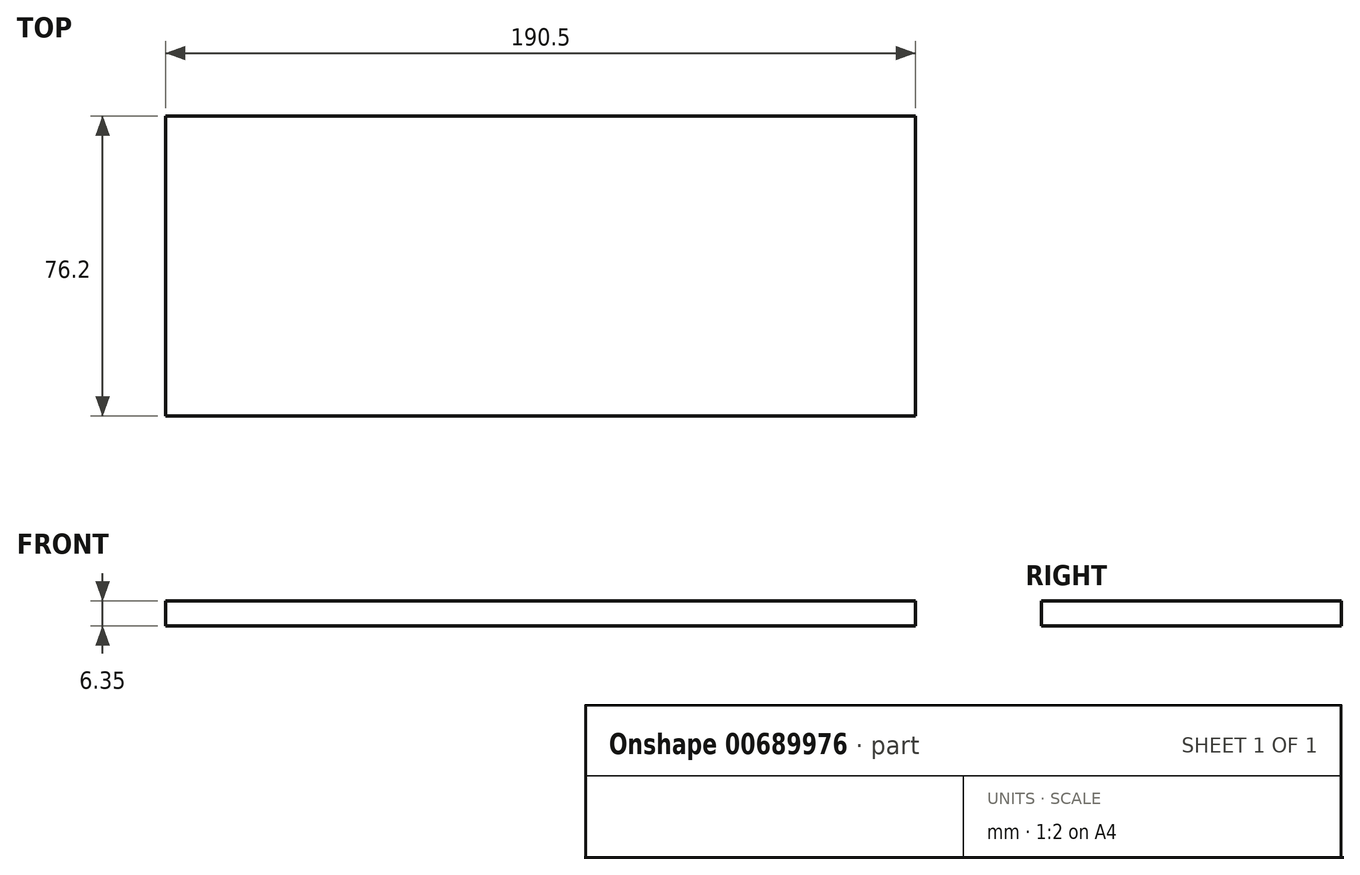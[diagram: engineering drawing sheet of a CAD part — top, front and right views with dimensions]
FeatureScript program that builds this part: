
annotation { "Feature Type Name" : "Feature", "Feature Type Description" : "" }
export const myFeature = defineFeature(function(context is Context, id is Id, definition is map)
    precondition{}
    {
        {
            var Q0;
            Q0=qCreatedBy(makeId("Top.planeOp"),FACE);
            var sketch = newSketch(context, id + "F0", { "sketchPlane" : qUnion([Q0])});
            skLineSegment(sketch, "E0.bottom", {"start": v(-112.07, 36.71) * mm, "end": v(78.43, 36.71) * mm});
            skLineSegment(sketch, "E0.top", {"start": v(-112.07, -39.49) * mm, "end": v(78.43, -39.49) * mm});
            skLineSegment(sketch, "E0.left", {"start": v(-112.07, 36.71) * mm, "end": v(-112.07, -39.49) * mm});
            skLineSegment(sketch, "E0.right", {"start": v(78.43, 36.71) * mm, "end": v(78.43, -39.49) * mm});
            skSolve(sketch);
        }
        {
            var Q0;
            Q0 = qSketchRegion(id + "F0", true);
            extrude(context, id + "F1", {"entities" : qUnion([Q0]), "depth" : 6.35 * mm, "offsetDistance" : 25.4 * mm});
        }
    });
